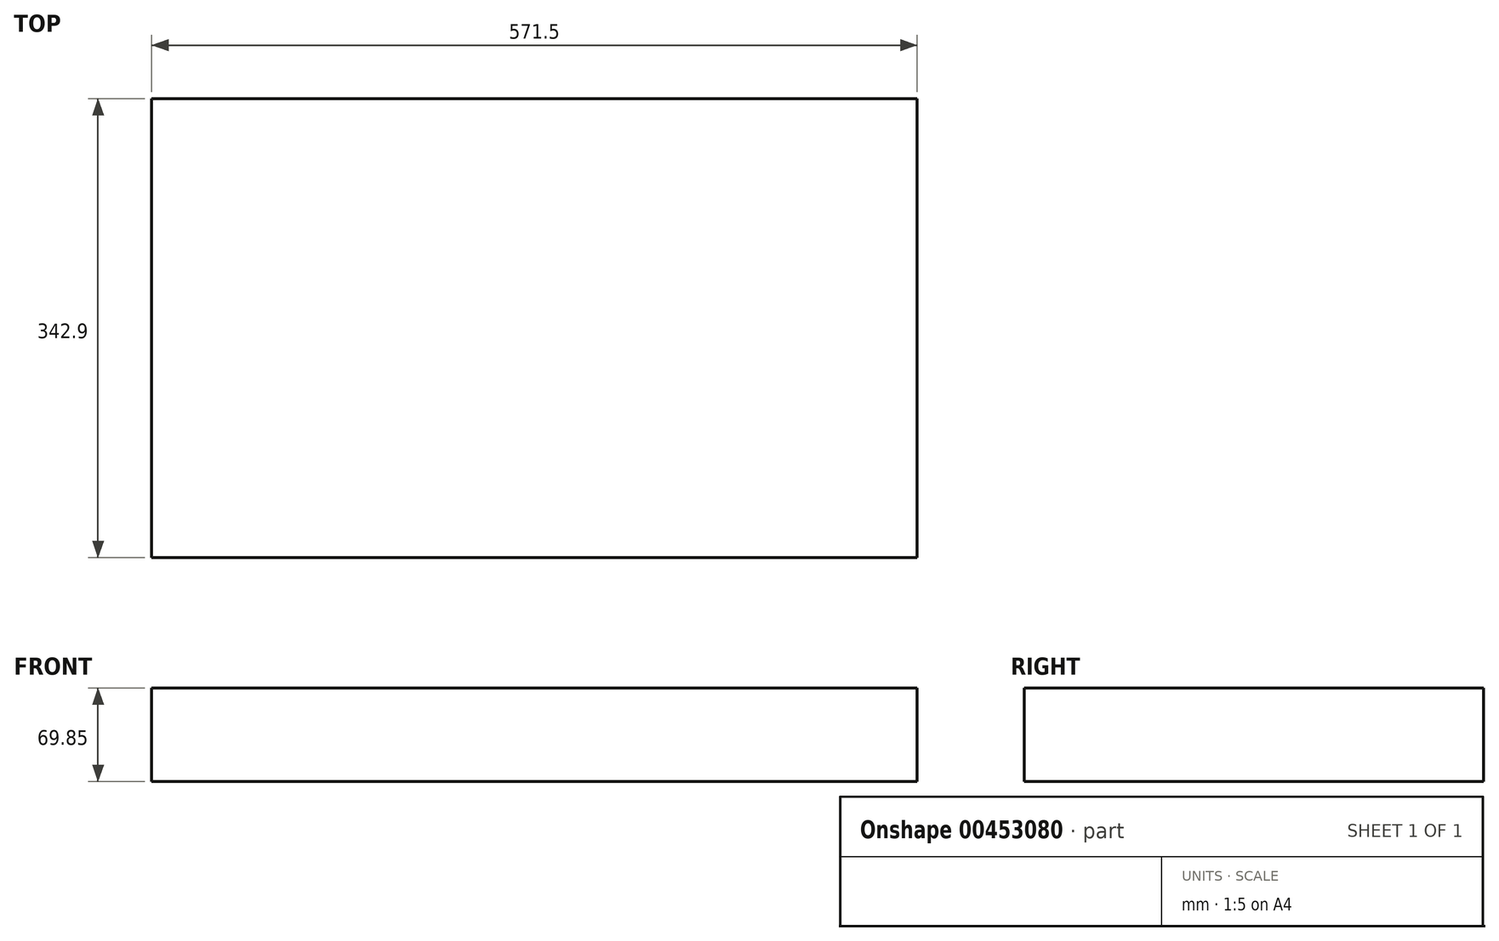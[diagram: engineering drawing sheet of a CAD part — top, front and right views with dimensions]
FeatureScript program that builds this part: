
annotation { "Feature Type Name" : "Feature", "Feature Type Description" : "" }
export const myFeature = defineFeature(function(context is Context, id is Id, definition is map)
    precondition{}
    {
        {
            var Q0;
            Q0=qCreatedBy(makeId("Top.planeOp"),FACE);
            var sketch = newSketch(context, id + "F0", { "sketchPlane" : qUnion([Q0])});
            skLineSegment(sketch, "E0.bottom", {"start": v(285.75, 171.45) * mm, "end": v(-285.75, 171.45) * mm});
            skLineSegment(sketch, "E0.top", {"start": v(285.75, -171.45) * mm, "end": v(-285.75, -171.45) * mm});
            skLineSegment(sketch, "E0.left", {"start": v(285.75, 171.45) * mm, "end": v(285.75, -171.45) * mm});
            skLineSegment(sketch, "E0.right", {"start": v(-285.75, 171.45) * mm, "end": v(-285.75, -171.45) * mm});
            skPoint(sketch, "E0.middle", {"position": v(0, 0) * mm});
            skSolve(sketch);
        }
        {
            var Q0;
            Q0 = qSketchRegion(id + "F0", true);
            extrude(context, id + "F1", {"entities" : qUnion([Q0]), "depth" : 69.85 * mm, "offsetDistance" : 25.4 * mm});
        }
    });
